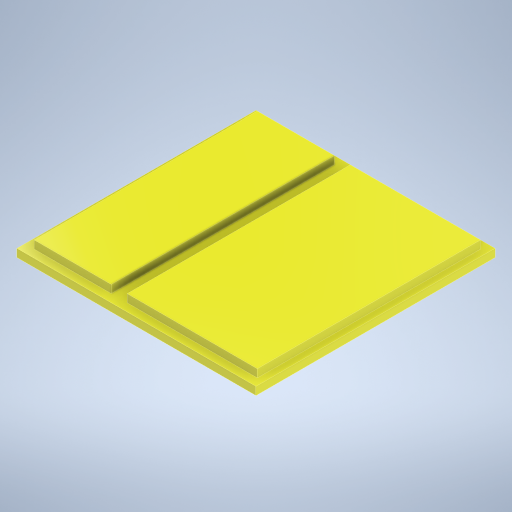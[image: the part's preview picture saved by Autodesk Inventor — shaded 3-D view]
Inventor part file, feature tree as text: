
AUTODESK INVENTOR PART (.ipt)
format: ipt  version: 2024 (Build 280153000, 153)  size: 257,024 bytes
history: native  units: mm
features: extrude x4, sketch x4, other x1
ambient origin geometry x8: Origin, YZ Plane, XZ Plane, XY Plane, X Axis, Y Axis, Z Axis, Center Point
bodies: Body1 (feature_tree)
feature tree (9):
  other  "Těleso1"
  extrude  "Vysunutí1"  Depth=90.0mm
  extrude  "Vysunutí2"  Depth=90.0mm
  extrude  "Vysunutí3"  Depth=3.0mm TaperAngle=0.0deg
  extrude  "Vysunutí4"  Depth=3.5mm
  sketch  "Náčrt1"
  sketch  "Náčrt2"
  sketch  "Náčrt3"
  sketch  "Náčrt6"
